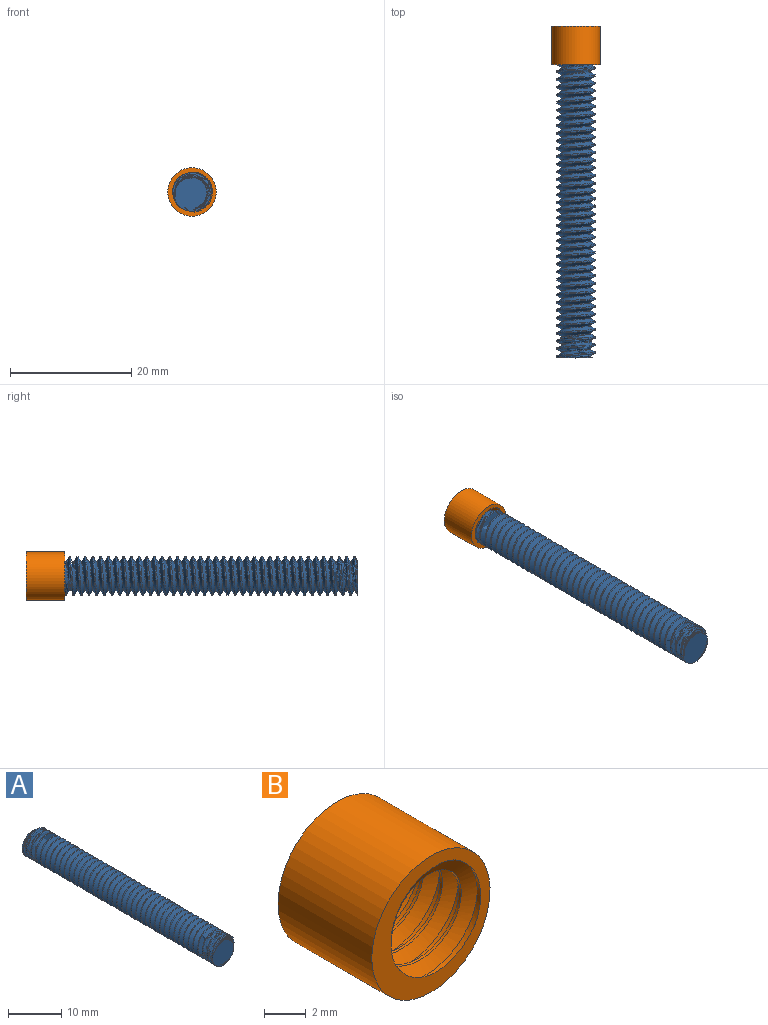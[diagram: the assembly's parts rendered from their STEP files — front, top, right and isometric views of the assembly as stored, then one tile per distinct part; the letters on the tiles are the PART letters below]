
ASSEMBLY  parts=2 mates=1
PART A: 6 faces, bbox 6.8x52.6x7.8 mm
  f0: cylinder r=3.17mm len=50.8mm, axis (0,1,0), area 168.2mm2, adj f1,f2,f3,f5
  f1: plane 6.12x6.1mm, normal (0,-1,0), area 24.9mm2, adj f0,f3,f4,f5
  f2: plane 6.12x6.1mm, normal (0,1,0), area 24.9mm2, adj f0,f3,f4,f5
  f3: bspline ~52.1x7.33mm, area 630.9mm2, adj f0,f1,f2,f4
  f4: cylinder r=2.4mm len=50.8mm, axis (0,1,0), area 98.6mm2, adj f1,f2,f3,f5
  f5: bspline ~51.88x7.33mm, area 629.7mm2, adj f0,f1,f2,f4
PART B: 7 faces, bbox 8.4x7.7x8.4 mm
  f0: plane 8.36x8.36mm, normal (0,-1,0), area 20.6mm2, adj f2,f3,f4,f5,f6
  f1: plane 8.36x8.36mm, normal (0,1,0), area 20.6mm2, adj f2,f3,f4,f5,f6
  f2: cylinder r=4mm len=8mm, axis (0,1,0), area 159.6mm2, adj f0,f1
  f3: cylinder r=2.67mm len=6.35mm, axis (0,-1,0), area 13.1mm2, adj f0,f1,f5,f6
  f4: cylinder r=3.36mm len=6.73mm, axis (0,1,0), area 32.5mm2, adj f0,f1,f5,f6
  f5: bspline ~7.77x7.17mm, area 75.4mm2, adj f0,f1,f3,f4
  f6: bspline ~7.77x7.38mm, area 75.4mm2, adj f0,f1,f3,f4
PLACE A rot(axis=(0,-1,0),41.5deg) t=(0,-3.98,0)mm
PLACE B at identity fixed
MATE cylindrical B.f2 <-> A.f0  axis (0,1,0) through (0,-6.35,0)mm
